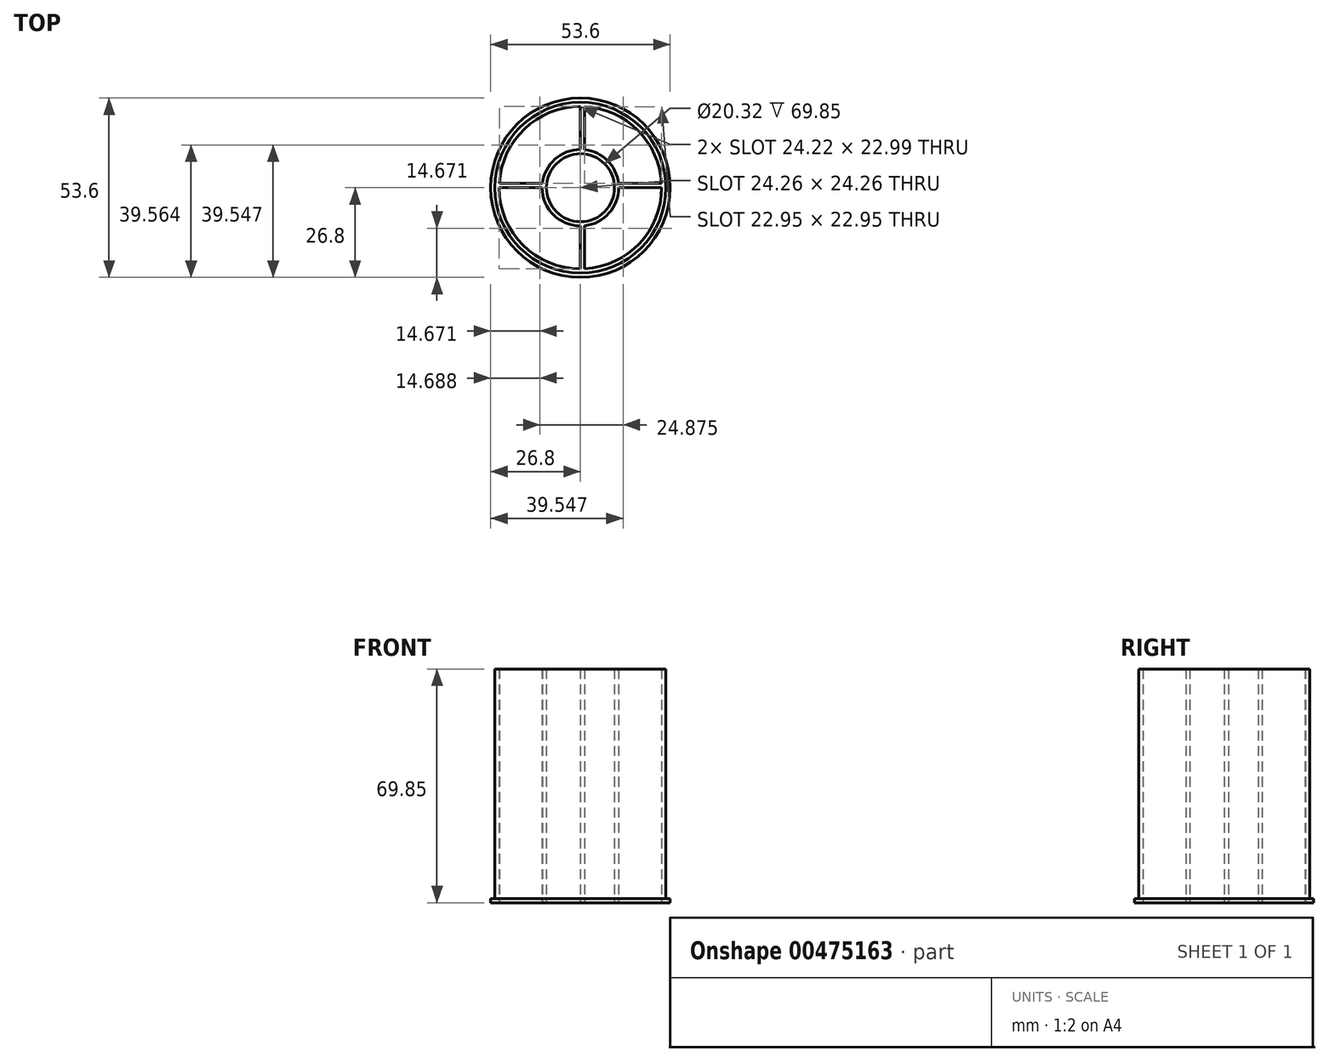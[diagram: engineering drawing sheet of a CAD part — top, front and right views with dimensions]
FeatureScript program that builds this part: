
annotation { "Feature Type Name" : "Feature", "Feature Type Description" : "" }
export const myFeature = defineFeature(function(context is Context, id is Id, definition is map)
    precondition{}
    {
        {
            var Q0;
            Q0=qCreatedBy(makeId("Top.planeOp"),FACE);
            var sketch = newSketch(context, id + "F0", { "sketchPlane" : qUnion([Q0])});
            skCircle(sketch, "E0", {"center": v(0, 0) * mm, "radius": 24.26 * mm});
            skCircle(sketch, "E1", {"center": v(0, 0) * mm, "radius": 11.43 * mm});
            skCircle(sketch, "E2.0", {"center": v(0, 0) * mm, "radius": 25.53 * mm});
            skCircle(sketch, "E3.0", {"center": v(0, 0) * mm, "radius": 10.16 * mm});
            skLineSegment(sketch, "E4", {"start": v(0, 24.26) * mm, "end": v(0, 11.43) * mm});
            skLineSegment(sketch, "E5", {"start": v(1.27, 24.22) * mm, "end": v(1.27, 11.36) * mm});
            skLineSegment(sketch, "E6", {"start": v(11.36, 1.27) * mm, "end": v(24.22, 1.27) * mm});
            skLineSegment(sketch, "E7", {"start": v(11.43, 0) * mm, "end": v(24.26, 0) * mm});
            skLineSegment(sketch, "E8", {"start": v(0, -11.43) * mm, "end": v(0, -24.26) * mm});
            skLineSegment(sketch, "E9", {"start": v(1.27, -11.36) * mm, "end": v(1.27, -24.22) * mm});
            skLineSegment(sketch, "E10", {"start": v(-11.43, 0) * mm, "end": v(-24.26, 0) * mm});
            skLineSegment(sketch, "E11", {"start": v(-24.22, 1.27) * mm, "end": v(-11.36, 1.27) * mm});
            skCircle(sketch, "E12.0", {"center": v(0, 0) * mm, "radius": 26.8 * mm});
            skPoint(sketch, "E13.centerSnap0", {"position": v(1.27, 17.8) * mm});
            skPoint(sketch, "E14.centerSnap0", {"position": v(-17.8, 1.27) * mm});
            skPoint(sketch, "E15.centerSnap0", {"position": v(17.8, 1.27) * mm});
            skSolve(sketch);
        }
        {
            var Q0;
            Q0=makeQuery(id+"F0.imprint","IMPRINT",FACE,{"disambiguationData":[TD([[makeQuery(id+"F0.imprint","IMPRINT",EDGE,{"derivedFrom":sQuery(id+"F0.wireOp",EDGE,"E2.0")}),1.0]])]});
            var Q1;
            Q1=makeQuery(id+"F0.imprint","IMPRINT",FACE,{"disambiguationData":[TD([[makeQuery(id+"F0.imprint","IMPRINT",EDGE,{"derivedFrom":sQuery(id+"F0.wireOp",EDGE,"E3.0")}),-1.0]])]});
            var Q2;
            {var subQ0=sQuery(id+"F0.wireOp",EDGE,"E4");Q2=makeQuery(id+"F0.imprint","IMPRINT",FACE,{"disambiguationData":[TD([[makeQuery(id+"F0.imprint","IMPRINT",EDGE,{"derivedFrom":subQ0}),1.0]])]});}
            var Q3;
            {var subQ0=sQuery(id+"F0.wireOp",EDGE,"E6");Q3=makeQuery(id+"F0.imprint","IMPRINT",FACE,{"disambiguationData":[TD([[makeQuery(id+"F0.imprint","IMPRINT",EDGE,{"derivedFrom":subQ0}),-1.0]])]});}
            var Q4;
            {var subQ0=sQuery(id+"F0.wireOp",EDGE,"E8");Q4=makeQuery(id+"F0.imprint","IMPRINT",FACE,{"disambiguationData":[TD([[makeQuery(id+"F0.imprint","IMPRINT",EDGE,{"derivedFrom":subQ0}),1.0]])]});}
            var Q5;
            {var subQ0=sQuery(id+"F0.wireOp",EDGE,"E10");Q5=makeQuery(id+"F0.imprint","IMPRINT",FACE,{"disambiguationData":[TD([[makeQuery(id+"F0.imprint","IMPRINT",EDGE,{"derivedFrom":subQ0}),-1.0]])]});}
            extrude(context, id + "F1", {"entities" : qUnion([Q0, Q1, Q2, Q3, Q4, Q5]), "depth" : 69.85 * mm});
        }
        {
            var Q0;
            Q0 = qSketchRegion(id + "F0", true);
            extrude(context, id + "F2", {"entities" : qUnion([Q0]), "operationType" : NewBodyOperationType.ADD, "depth" : 1.27 * mm});
        }
    });
